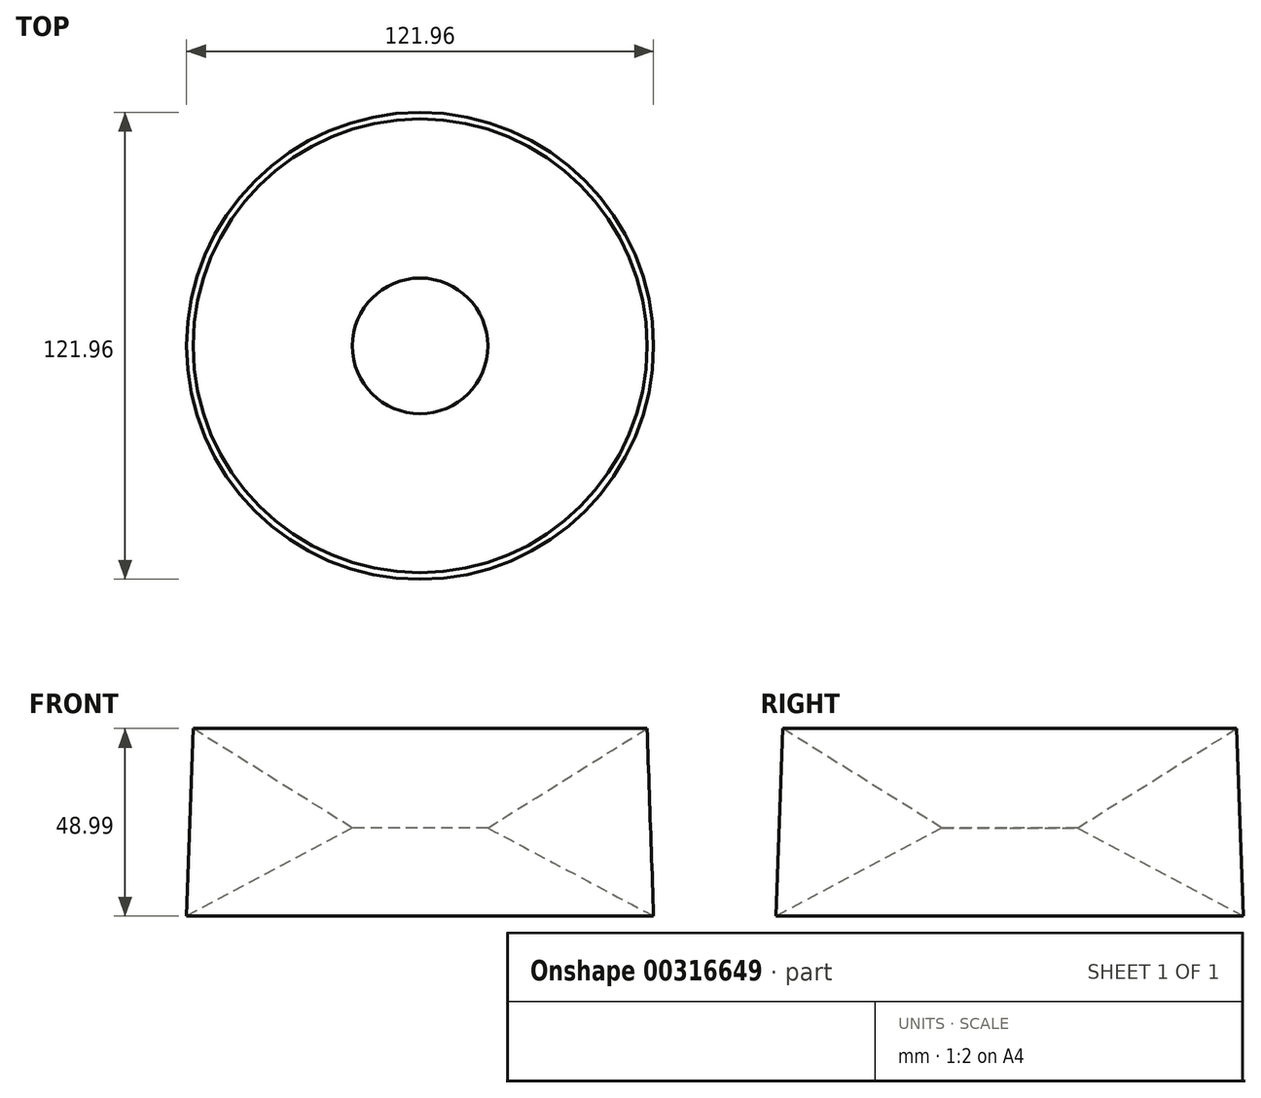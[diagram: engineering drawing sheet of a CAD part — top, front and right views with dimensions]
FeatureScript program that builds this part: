
annotation { "Feature Type Name" : "Feature", "Feature Type Description" : "" }
export const myFeature = defineFeature(function(context is Context, id is Id, definition is map)
    precondition{}
    {
        {
            var Q0;
            Q0=qCreatedBy(makeId("Front.planeOp"),FACE);
            var sketch = newSketch(context, id + "F0", { "sketchPlane" : qUnion([Q0])});
            skLineSegment(sketch, "E0", {"start": v(0, 70.44) * mm, "end": v(0, -61.93) * mm, "construction": true});
            skCircle(sketch, "E1.cCircle", {"center": v(-45.99, 41.73) * mm, "radius": 14.15 * mm, "construction": true});
            skLineSegment(sketch, "E1.0", {"start": v(-17.7, 40.75) * mm, "end": v(-60.98, 17.73) * mm});
            skLineSegment(sketch, "E1.1", {"start": v(-60.98, 17.73) * mm, "end": v(-59.28, 66.72) * mm});
            skLineSegment(sketch, "E1.2", {"start": v(-59.28, 66.72) * mm, "end": v(-17.7, 40.75) * mm});
            skPoint(sketch, "E1.0.midPoint", {"position": v(-39.34, 29.24) * mm});
            skSolve(sketch);
        }
        {
            var Q0;
            Q0=makeQuery(id+"F0.imprint","IMPRINT",FACE,{"disambiguationData":[TD([[makeQuery(id+"F0.imprint","IMPRINT",EDGE,{"derivedFrom":sQuery(id+"F0.wireOp",EDGE,"E1.0")}),-1.0]])]});
            var Q1;
            Q1=sQuery(id+"F0.wireOp",EDGE,"E0");
            revolve(context, id + "F1", {"entities" : qUnion([Q0]), "axis" : qUnion([Q1]), "revolveType" : RevolveType.FULL});
        }
    });
